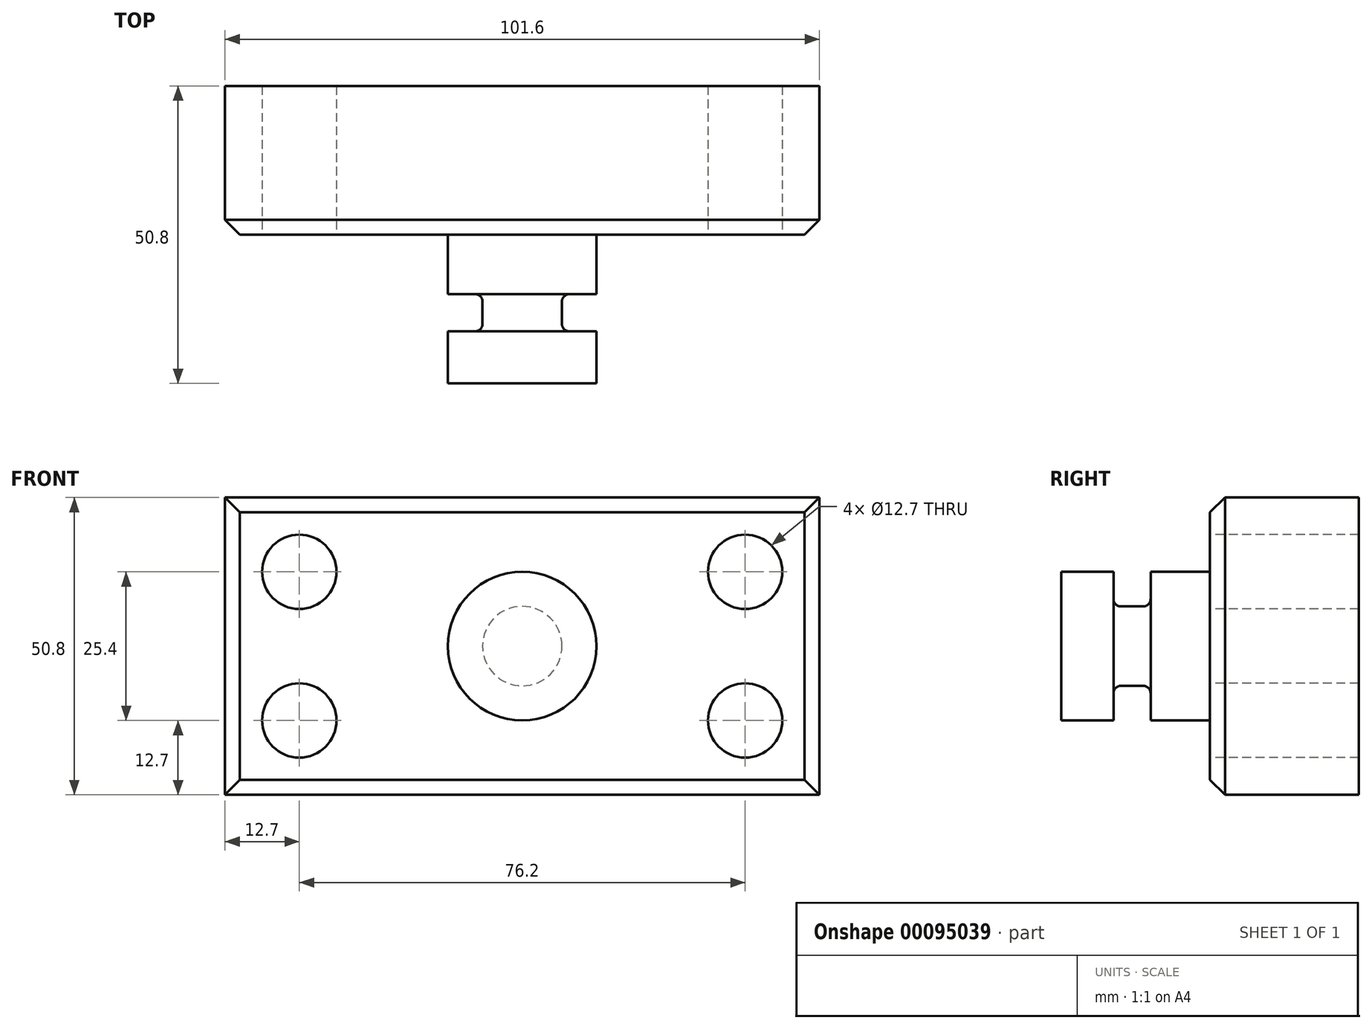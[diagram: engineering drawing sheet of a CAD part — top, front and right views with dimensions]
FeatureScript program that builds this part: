
annotation { "Feature Type Name" : "Feature", "Feature Type Description" : "" }
export const myFeature = defineFeature(function(context is Context, id is Id, definition is map)
    precondition{}
    {
        {
            var Q0;
            Q0=qCreatedBy(makeId("Front.planeOp"),FACE);
            var sketch = newSketch(context, id + "F0", { "sketchPlane" : qUnion([Q0])});
            skLineSegment(sketch, "E0.bottom", {"start": v(50.8, 25.4) * mm, "end": v(-50.8, 25.4) * mm});
            skLineSegment(sketch, "E0.top", {"start": v(50.8, -25.4) * mm, "end": v(-50.8, -25.4) * mm});
            skLineSegment(sketch, "E0.left", {"start": v(50.8, 25.4) * mm, "end": v(50.8, -25.4) * mm});
            skLineSegment(sketch, "E0.right", {"start": v(-50.8, 25.4) * mm, "end": v(-50.8, -25.4) * mm});
            skPoint(sketch, "E0.middle", {"position": v(0, 0) * mm});
            skSolve(sketch);
        }
        {
            var Q0;
            Q0=makeQuery(id+"F0.imprint","IMPRINT",FACE,{"disambiguationData":[TD([[makeQuery(id+"F0.imprint","IMPRINT",EDGE,{"derivedFrom":sQuery(id+"F0.wireOp",EDGE,"E0.bottom")}),1.0]])]});
            extrude(context, id + "F1", {"entities" : qUnion([Q0]), "depth" : 25.4 * mm});
        }
        {
            var Q0;
            Q0=makeQuery(id+"F1.opExtrude","CAP_FACE",FACE,{"disambiguationData":[OSD([sQuery(id+"F0.wireOp",EDGE,"E0.bottom"),sQuery(id+"F0.wireOp",EDGE,"E0.top"),sQuery(id+"F0.wireOp",EDGE,"E0.left"),sQuery(id+"F0.wireOp",EDGE,"E0.right")])],"isStart":false});
            var sketch = newSketch(context, id + "F2", { "sketchPlane" : qUnion([Q0])});
            skCircle(sketch, "E1", {"center": v(-38.1, 12.7) * mm, "radius": 6.35 * mm});
            skCircle(sketch, "E2", {"center": v(-38.1, -12.7) * mm, "radius": 6.35 * mm});
            skCircle(sketch, "E3", {"center": v(38.1, -12.7) * mm, "radius": 6.35 * mm});
            skCircle(sketch, "E4", {"center": v(38.1, 12.7) * mm, "radius": 6.35 * mm});
            skSolve(sketch);
        }
        {
            var Q0;
            Q0=makeQuery(id+"F2.imprint","IMPRINT",FACE,{"disambiguationData":[TD([[makeQuery(id+"F2.imprint","IMPRINT",EDGE,{"derivedFrom":sQuery(id+"F2.wireOp",EDGE,"E1")}),1.0]])]});
            var Q1;
            Q1=makeQuery(id+"F2.imprint","IMPRINT",FACE,{"disambiguationData":[TD([[makeQuery(id+"F2.imprint","IMPRINT",EDGE,{"derivedFrom":sQuery(id+"F2.wireOp",EDGE,"E2")}),1.0]])]});
            var Q2;
            Q2=makeQuery(id+"F2.imprint","IMPRINT",FACE,{"disambiguationData":[TD([[makeQuery(id+"F2.imprint","IMPRINT",EDGE,{"derivedFrom":sQuery(id+"F2.wireOp",EDGE,"E4")}),1.0]])]});
            var Q3;
            Q3=makeQuery(id+"F2.imprint","IMPRINT",FACE,{"disambiguationData":[TD([[makeQuery(id+"F2.imprint","IMPRINT",EDGE,{"derivedFrom":sQuery(id+"F2.wireOp",EDGE,"E3")}),1.0]])]});
            var Q4;
            Q4=sQuery(id+"F2.wireOp",EDGE,"E1");
            extrude(context, id + "F3", {"entities" : qUnion([Q0, Q1, Q2, Q3]), "operationType" : NewBodyOperationType.REMOVE, "surfaceEntities" : qUnion([Q4]), "endBound" : BoundingType.THROUGH_ALL, "oppositeDirection" : true, "depth" : 25.4 * mm});
        }
        {
            var Q0;
            Q0=qCreatedBy(makeId("Top.planeOp"),FACE);
            var sketch = newSketch(context, id + "F4", { "sketchPlane" : qUnion([Q0])});
            skLineSegment(sketch, "E5.bottom", {"start": v(12.7, -50.8) * mm, "end": v(0, -50.8) * mm});
            skLineSegment(sketch, "E5.top", {"start": v(12.7, -25.4) * mm, "end": v(0, -25.4) * mm});
            skLineSegment(sketch, "E5.left", {"start": v(12.7, -50.8) * mm, "end": v(12.7, -25.4) * mm});
            skLineSegment(sketch, "E5.right", {"start": v(0, -50.8) * mm, "end": v(0, -25.4) * mm});
            skSolve(sketch);
        }
        {
            var Q0;
            Q0=makeQuery(id+"F4.imprint","IMPRINT",FACE,{"disambiguationData":[TD([[makeQuery(id+"F4.imprint","IMPRINT",EDGE,{"derivedFrom":sQuery(id+"F4.wireOp",EDGE,"E5.bottom")}),-1.0]])]});
            var Q1;
            Q1=sQuery(id+"F4.wireOp",EDGE,"E5.right");
            revolve(context, id + "F5", {"operationType" : NewBodyOperationType.ADD, "entities" : qUnion([Q0]), "axis" : qUnion([Q1]), "revolveType" : RevolveType.FULL});
        }
        {
            var Q0;
            Q0=qCreatedBy(makeId("Top.planeOp"),FACE);
            var sketch = newSketch(context, id + "F6", { "sketchPlane" : qUnion([Q0])});
            skLineSegment(sketch, "E6.bottom", {"start": v(16.95, -41.91) * mm, "end": v(6.79, -41.91) * mm});
            skLineSegment(sketch, "E6.top", {"start": v(16.95, -35.56) * mm, "end": v(6.79, -35.56) * mm});
            skLineSegment(sketch, "E6.left", {"start": v(16.95, -41.91) * mm, "end": v(16.95, -35.56) * mm});
            skLineSegment(sketch, "E6.right", {"start": v(6.79, -41.91) * mm, "end": v(6.79, -35.56) * mm});
            skLineSegment(sketch, "E7", {"start": v(0, 0) * mm, "end": v(0, -72.44) * mm, "construction": true});
            skSolve(sketch);
        }
        {
            var Q0;
            Q0=makeQuery(id+"F6.imprint","IMPRINT",FACE,{"disambiguationData":[TD([[makeQuery(id+"F6.imprint","IMPRINT",EDGE,{"derivedFrom":sQuery(id+"F6.wireOp",EDGE,"E6.bottom")}),-1.0]])]});
            var Q1;
            Q1=sQuery(id+"F6.wireOp",EDGE,"E7");
            revolve(context, id + "F7", {"operationType" : NewBodyOperationType.REMOVE, "entities" : qUnion([Q0]), "axis" : qUnion([Q1]), "revolveType" : RevolveType.FULL, "oppositeDirection" : true});
        }
        {
            var Q0;
            Q0=makeQuery(id+"F5.opRevolve","SWEPT_EDGE",EDGE,{"disambiguationData":[OSD([sQuery(id+"F4.wireOp",EDGE,"E5.top"),sQuery(id+"F4.wireOp",EDGE,"E5.left")])]});
            var Q1;
            Q1=makeQuery(id+"F7.boolean.opBoolean","COPY",EDGE,{"derivedFrom":makeQuery(id+"F7.opRevolve","SWEPT_EDGE",EDGE,{"disambiguationData":[OSD([sQuery(id+"F6.wireOp",EDGE,"E6.bottom"),sQuery(id+"F6.wireOp",EDGE,"E6.right")])]})});
            var Q2;
            Q2=makeQuery(id+"F7.boolean.opBoolean","COPY",EDGE,{"derivedFrom":makeQuery(id+"F7.opRevolve","SWEPT_EDGE",EDGE,{"disambiguationData":[OSD([sQuery(id+"F6.wireOp",EDGE,"E6.top"),sQuery(id+"F6.wireOp",EDGE,"E6.right")])]})});
            fillet(context, id + "F8", {"entities" : qUnion([Q0, Q1, Q2]), "radius" : 1.27 * mm, "tangentPropagation" : true, "allowEdgeOverflow" : false});
        }
        {
            var Q0;
            Q0=makeQuery(id+"F1.opExtrude","CAP_EDGE",EDGE,{"disambiguationData":[OSD([sQuery(id+"F0.wireOp",EDGE,"E0.top")])],"isStart":false});
            var Q1;
            Q1=makeQuery(id+"F1.opExtrude","CAP_EDGE",EDGE,{"disambiguationData":[OSD([sQuery(id+"F0.wireOp",EDGE,"E0.bottom")])],"isStart":false});
            var Q2;
            Q2=makeQuery(id+"F1.opExtrude","CAP_EDGE",EDGE,{"disambiguationData":[OSD([sQuery(id+"F0.wireOp",EDGE,"E0.right")])],"isStart":false});
            var Q3;
            Q3=makeQuery(id+"F1.opExtrude","CAP_EDGE",EDGE,{"disambiguationData":[OSD([sQuery(id+"F0.wireOp",EDGE,"E0.left")])],"isStart":false});
            chamfer(context, id + "F9", {"entities" : qUnion([Q0, Q1, Q2, Q3]), "width" : 2.54 * mm, "tangentPropagation" : true});
        }
    });
